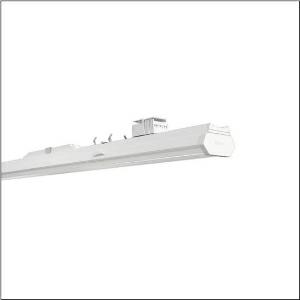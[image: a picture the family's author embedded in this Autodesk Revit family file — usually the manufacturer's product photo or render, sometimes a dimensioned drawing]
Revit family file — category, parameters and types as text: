
# Revit family: licross_r__11_protected_ho_51td12cn4exm_9b5e
name_source: partatom
category: Lighting Fixtures
units: mm (PartAtom-declared; Revit-internal decimal feet)

## family parameters
Cut with Voids When Loaded = No
Host = Face
Light Source = No
Part Type = Normal
Room Calculation Point = No
Round Connector Dimension = Use Diameter
Shared = No

## types (1)
- --- (1 x LED, 14240 lm, 77.6 W, 4000K)
    Apparent Load = 78 VA
    CIE Flux Codes = 70 91 97 98 100
    Color Rendering = 80
    Color Temperature = 4000K
    Default Elevation = 1800 mm
    Description = Licross® 11 Protected HO, luminaire insert, of sheet steel, galvanised, coil coated, white, length: 1.500mm, width: 90mm, height: 101mm, LED rated luminous flux: 14.240lm, light colour: 840, control gear: ON/OFF Multilumen, CLOi, with plug, 3-pole, with phase selection, mains connection: 220..240V, AC, 50/60Hz, start of lifetime: 78W, end of service life: 87W, halogen-free wiring, primary light control with lens, of plastic, primary optical cover: cover, of PMMA, light emission: direct distribution, primary light characteristic: symmetric, protection rating (complete): IP54, insulation class (complete): insulation class I (protective earthing), certification: CE, ENEC, VDE, UKCA, protection symbol: D if used in an environment with non-conductive dust loads with corresponding accessories, impact resistance: IK06, permissible ambient temperature for indoor applications: -35..+35°C, corresponds to IFS (International Featured Standards) requirements for safety and quality in the food industry, reducing of maximum allowable ambient temperature of 5°C with ceiling mounting, LABS conformity tested according to VDMA 24364:2018-05, packaging unit: 1 piece
    Height = 92 mm
    Lamp = 1 x LED
    Lamp Light Flux = 14240 lm
    Lamp Power = 77.6 W
    Lamp count = 1
    Length = 1500 mm
    Luminous efficacy = 184 lm/W
    Manufacturer = Siteco
    ModVariant = No
    Model = 51TD12CN4EXM
    Mounting Place = Ceiling
    Mounting Type = Pendant
    Number of Poles = 1
    OnlyDefault = Yes
    Power Factor = 1
    Product Name = Licross® 11 Protected HO
    Product group = luminaire insert
    ProductGroupID = 902
    Protection Class = Protection class I
    Protection Degree = IP 54
    RLX_Detail_Level = 1
    RLX_Emergency_Light_Flux = 0 lm
    RLX_Emergency_Type = 0
    RLX_Emergency_Type_DB = No
    RlxData = <blob elided: 22101 chars, md5=42b11e1d>
    Socket = socket
    Standby Power = 0 W
    System Light Flux = 14240 lm
    System Power = 78 W
    Type Comments = factory setting: luminous flux: 100 % | (A | C | E) | 181 mA
    Type Image = l_1256145.jpg
    URL = http://relux.com
    VarID = @adj_085956
    Voltage = 0 V
    Weight = 0.00 kg
    Width = 88 mm

## geometry (parser evidence)
native form markers: Blend x4, Sweep x9
no freeform markers — native parametric forms only
